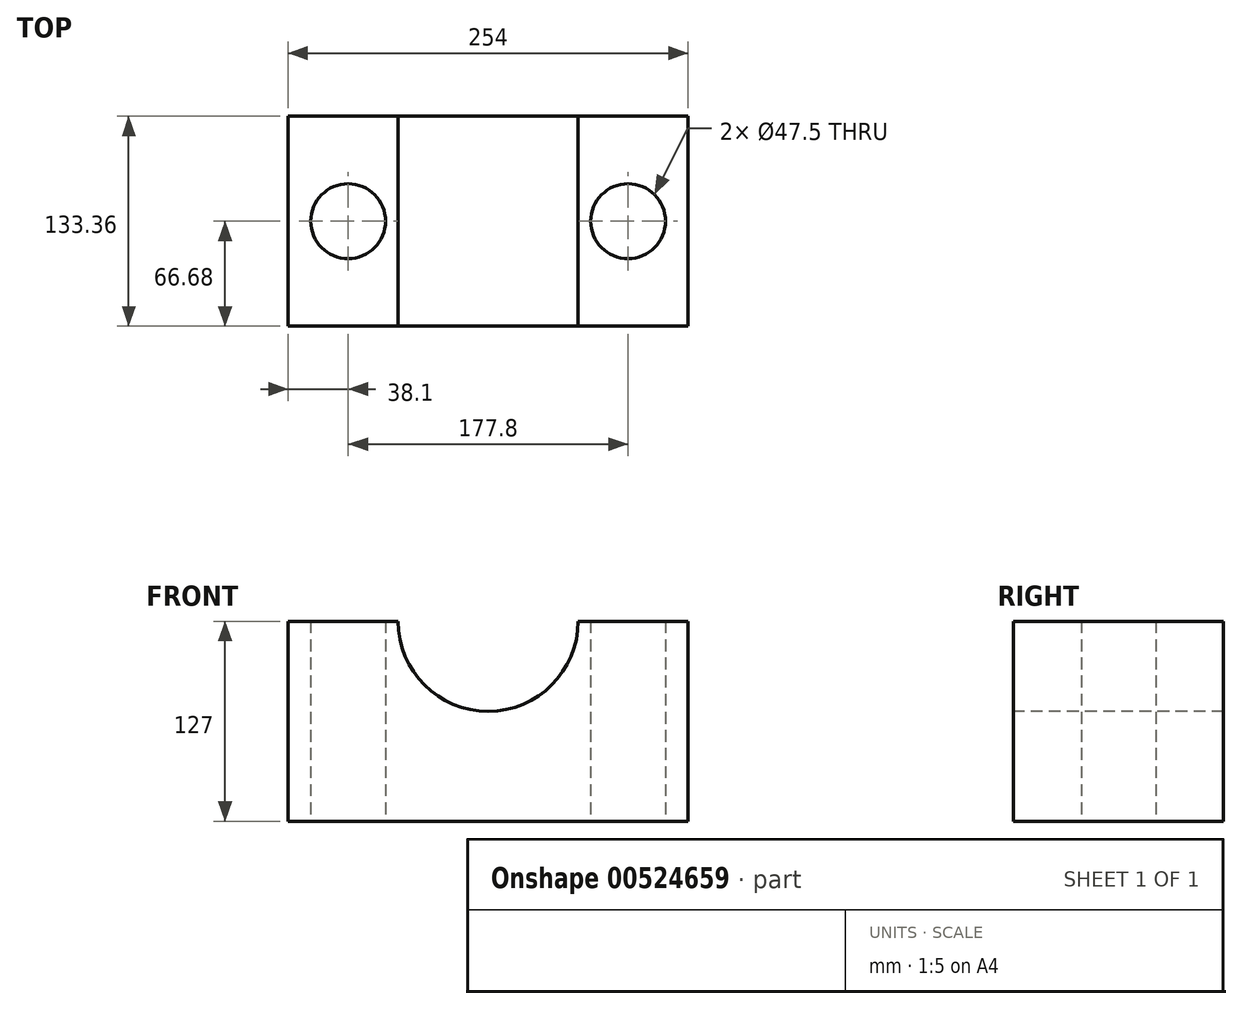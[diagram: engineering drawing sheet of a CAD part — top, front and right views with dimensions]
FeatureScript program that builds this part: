
annotation { "Feature Type Name" : "Feature", "Feature Type Description" : "" }
export const myFeature = defineFeature(function(context is Context, id is Id, definition is map)
    precondition{}
    {
        {
            var Q0;
            Q0=qCreatedBy(makeId("Top.planeOp"),FACE);
            var sketch = newSketch(context, id + "F0", { "sketchPlane" : qUnion([Q0])});
            skLineSegment(sketch, "E0.bottom", {"start": v(127, -66.68) * mm, "end": v(-127, -66.68) * mm});
            skLineSegment(sketch, "E0.top", {"start": v(127, 66.68) * mm, "end": v(-127, 66.68) * mm});
            skLineSegment(sketch, "E0.left", {"start": v(127, -66.68) * mm, "end": v(127, 66.67) * mm});
            skLineSegment(sketch, "E0.right", {"start": v(-127, -66.68) * mm, "end": v(-127, 66.67) * mm});
            skPoint(sketch, "E0.middle", {"position": v(0, 0) * mm});
            skCircle(sketch, "E1", {"center": v(-88.9, 0) * mm, "radius": 23.75 * mm});
            skCircle(sketch, "E2", {"center": v(88.9, 0) * mm, "radius": 23.75 * mm});
            skSolve(sketch);
        }
        {
            var Q0;
            Q0=makeQuery(id+"F0.imprint","IMPRINT",FACE,{"disambiguationData":[TD([[makeQuery(id+"F0.imprint","IMPRINT",EDGE,{"derivedFrom":sQuery(id+"F0.wireOp",EDGE,"E0.bottom")}),-1.0]])]});
            extrude(context, id + "F1", {"entities" : qUnion([Q0]), "depth" : 127 * mm, "offsetDistance" : 25.4 * mm});
        }
        {
            var Q0;
            Q0=makeQuery(id+"F1.opExtrude","SWEPT_FACE",FACE,{"disambiguationData":[OSD([sQuery(id+"F0.wireOp",EDGE,"E0.bottom")])]});
            var sketch = newSketch(context, id + "F2", { "sketchPlane" : qUnion([Q0])});
            skCircle(sketch, "E3", {"center": v(0, 127) * mm, "radius": 57.15 * mm});
            skSolve(sketch);
        }
        {
            var Q0;
            {var subQ0=sQuery(id+"F2.wireOp",EDGE,"E3");var subQ1=makeQuery(id+"F1.opExtrude","CAP_EDGE",EDGE,{"disambiguationData":[OSD([sQuery(id+"F0.wireOp",EDGE,"E0.bottom")])],"isStart":false});var subQ2=makeQuery(id+"F2.imprint","INTERSECT",VERTEX,{"disambiguationData":[OD(0.0)],"derivedFrom":[subQ1,subQ0]});Q0=makeQuery(id+"F2.imprint","IMPRINT",FACE,{"disambiguationData":[TD([[makeQuery(id+"F2.imprint","IMPRINT",EDGE,{"disambiguationData":[TD([[subQ2,-1.0]])],"derivedFrom":subQ0}),1.0]])]});}
            var Q1;
            {var subQ0=sQuery(id+"F2.wireOp",EDGE,"E3");var subQ1=makeQuery(id+"F1.opExtrude","CAP_EDGE",EDGE,{"disambiguationData":[OSD([sQuery(id+"F0.wireOp",EDGE,"E0.bottom")])],"isStart":false});var subQ2=makeQuery(id+"F2.imprint","INTERSECT",VERTEX,{"disambiguationData":[OD(0.0)],"derivedFrom":[subQ1,subQ0]});Q1=makeQuery(id+"F2.imprint","IMPRINT",FACE,{"disambiguationData":[TD([[makeQuery(id+"F2.imprint","IMPRINT",EDGE,{"disambiguationData":[TD([[subQ2,1.0]])],"derivedFrom":subQ0}),1.0]])]});}
            extrude(context, id + "F3", {"entities" : qUnion([Q0, Q1]), "operationType" : NewBodyOperationType.REMOVE, "endBound" : BoundingType.THROUGH_ALL, "oppositeDirection" : true, "depth" : 25.4 * mm, "offsetDistance" : 25.4 * mm});
        }
    });
